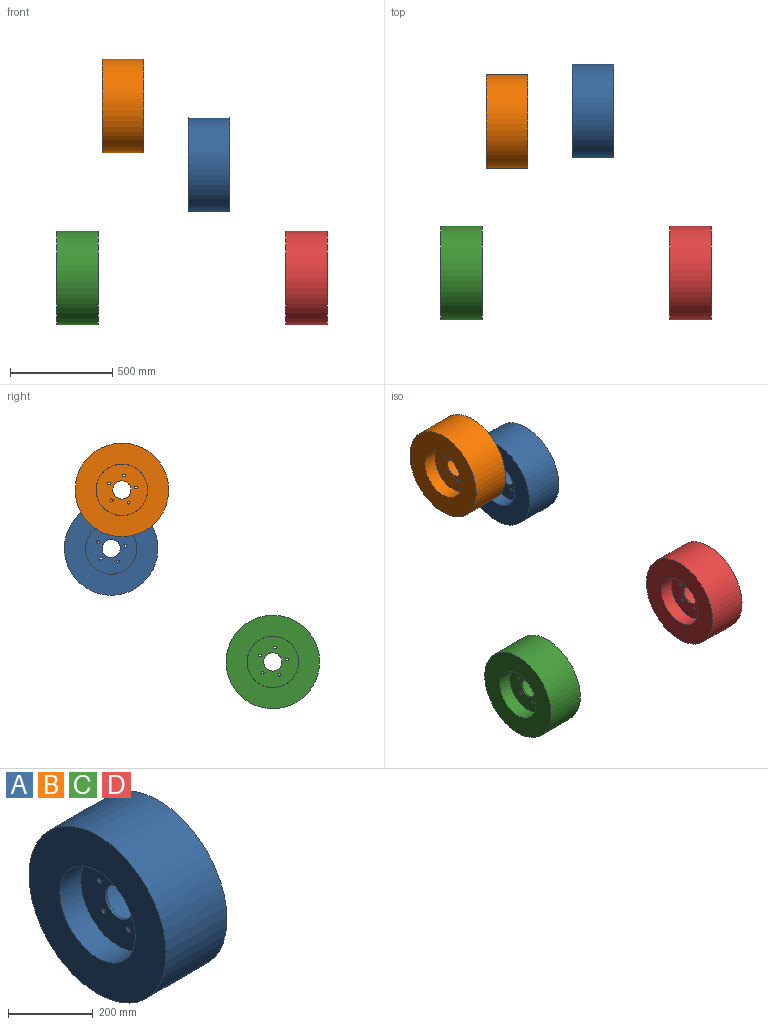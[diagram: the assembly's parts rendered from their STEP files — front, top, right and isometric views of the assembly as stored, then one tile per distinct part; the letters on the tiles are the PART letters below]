
ASSEMBLY  parts=4 mates=1
PART A: 13 faces, bbox 203.2x457.2x457.2 mm
  f0: cylinder r=125.59mm len=251.18mm, axis (-1,0,0), area 100217.2mm2, adj f3,f12
  f1: cylinder r=125.59mm len=251.18mm, axis (-1,0,0), area 55119.5mm2, adj f4,f11
  f2: cylinder r=228.6mm len=457.2mm, axis (-1,0,0), area 291863.5mm2, adj f3,f4
  f3: plane 457.2x457.2mm, normal (1,0,0), area 114620.5mm2, adj f0,f2
  f4: plane 457.2x457.2mm, normal (-1,0,0), area 114620.5mm2, adj f1,f2
  f5: cylinder r=6.35mm len=12.7mm, axis (1,0,0), area 253.4mm2, adj f11,f12
  f6: cylinder r=6.35mm len=12.7mm, axis (1,0,0), area 253.4mm2, adj f11,f12
  f7: cylinder r=6.35mm len=12.7mm, axis (1,0,0), area 253.4mm2, adj f11,f12
  f8: cylinder r=6.35mm len=12.7mm, axis (1,0,0), area 253.4mm2, adj f11,f12
  f9: cylinder r=6.35mm len=12.7mm, axis (1,0,0), area 253.4mm2, adj f11,f12
  f10: cylinder r=44.47mm len=88.93mm, axis (1,0,0), area 1774.1mm2, adj f11,f12
  f11: plane 251.18x251.18mm, normal (-1,0,0), area 42707.9mm2, adj f1,f5,f6,f7,f8,f9,f10
  f12: plane 251.18x251.18mm, normal (1,0,0), area 42707.9mm2, adj f0,f5,f6,f7,f8,f9,f10
PART B: same geometry as A
PART C: same geometry as A
PART D: same geometry as A
PLACE A t=(603.23,574.17,338.84)mm
PLACE B t=(181.76,521.67,625.1)mm
PLACE C rot(axis=(0.26,0.3,0.92),0deg) t=(-38.98,-216.05,-215.81)mm
PLACE D rot(axis=(0.26,0.3,0.92),0deg) t=(1078.62,-216.05,-215.81)mm
MATE fastened D.f0 <-> C.f0  axis (-1,0,0) through (1078.62,257.83,8.26)mm
